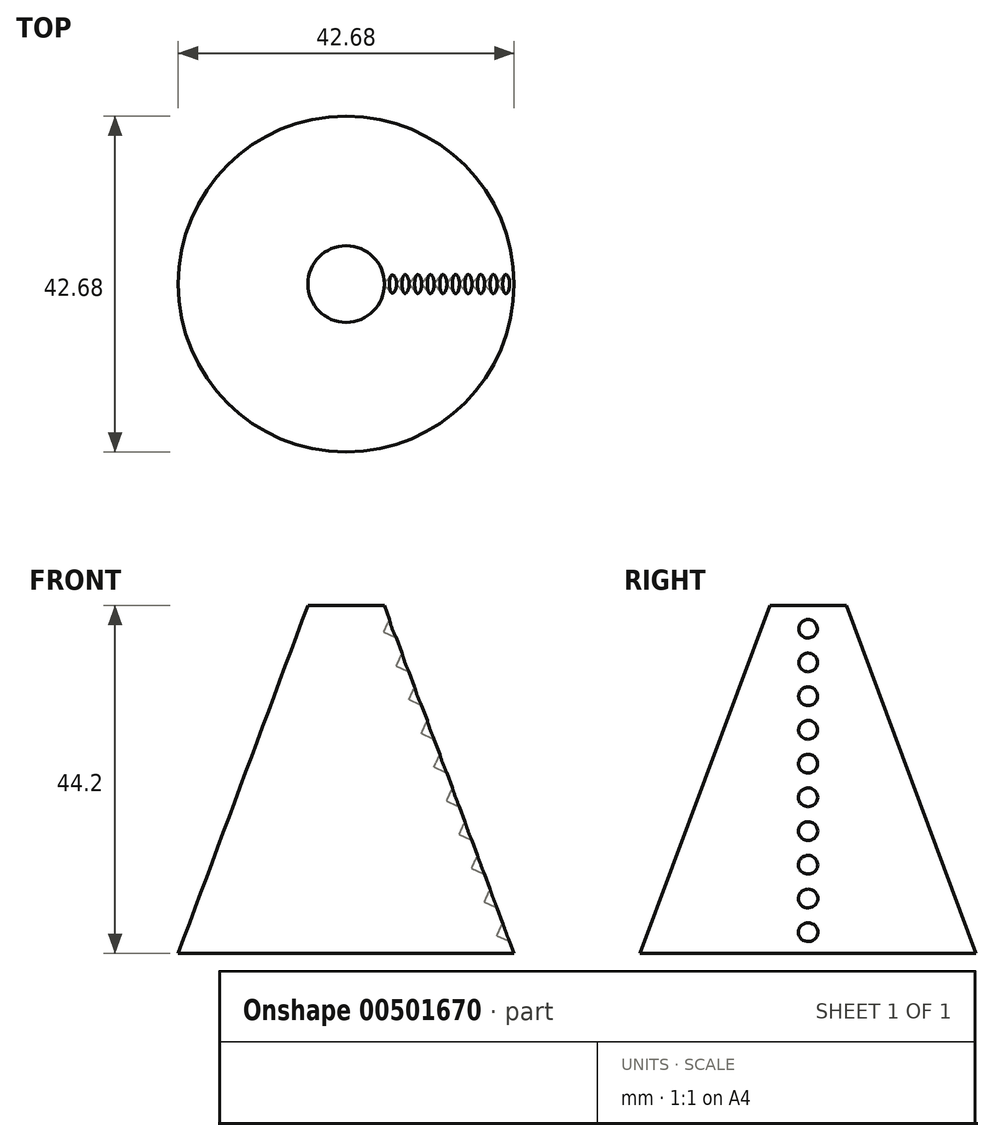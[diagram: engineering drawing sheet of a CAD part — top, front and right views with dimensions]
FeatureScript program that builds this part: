
annotation { "Feature Type Name" : "Feature", "Feature Type Description" : "" }
export const myFeature = defineFeature(function(context is Context, id is Id, definition is map)
    precondition{}
    {
        {
            var Q0;
            Q0=qCreatedBy(makeId("Front.planeOp"),FACE);
            var sketch = newSketch(context, id + "F0", { "sketchPlane" : qUnion([Q0])});
            skLineSegment(sketch, "E0", {"start": v(0, 0) * mm, "end": v(0, 44.2) * mm});
            skLineSegment(sketch, "E1", {"start": v(0, 44.2) * mm, "end": v(4.86, 44.2) * mm});
            skLineSegment(sketch, "E2", {"start": v(4.86, 44.2) * mm, "end": v(21.34, 0) * mm});
            skLineSegment(sketch, "E3", {"start": v(21.34, 0) * mm, "end": v(0, 0) * mm});
            skSolve(sketch);
        }
        {
            var Q0;
            Q0=makeQuery(id+"F0.imprint","IMPRINT",FACE,{"disambiguationData":[TD([[makeQuery(id+"F0.imprint","IMPRINT",EDGE,{"derivedFrom":sQuery(id+"F0.wireOp",EDGE,"E0")}),-1.0]])]});
            var Q1;
            Q1=sQuery(id+"F0.wireOp",EDGE,"E0");
            revolve(context, id + "F1", {"surfaceOperationType" : NewSurfaceOperationType.NEW, "entities" : qUnion([Q0]), "axis" : qUnion([Q1]), "revolveType" : RevolveType.FULL});
        }
        {
            var Q0;
            Q0=sQuery(id+"F0.wireOp",EDGE,"E2");
            cPlane(context, id + "F2", {"entities" : qUnion([Q0]), "cplaneType" : CPlaneType.LINE_ANGLE, "offset" : 25.4 * mm, "angle" : 0 * degree, "width" : 152.4 * mm, "height" : 152.4 * mm});
        }
        {
            var Q0;
            Q0=qCreatedBy(id+"F2.planeOp",FACE);
            var sketch = newSketch(context, id + "F3", { "sketchPlane" : qUnion([Q0])});
            skCircle(sketch, "E4", {"center": v(0, 36.58) * mm, "radius": 1.27 * mm});
            skCircle(sketch, "E5", {"center": v(0, 32) * mm, "radius": 1.27 * mm});
            skCircle(sketch, "E6", {"center": v(0, 27.43) * mm, "radius": 1.27 * mm});
            skCircle(sketch, "E7", {"center": v(0, 22.86) * mm, "radius": 1.27 * mm});
            skCircle(sketch, "E8", {"center": v(0, 18.29) * mm, "radius": 1.27 * mm});
            skCircle(sketch, "E9", {"center": v(0, 13.72) * mm, "radius": 1.27 * mm});
            skCircle(sketch, "E10", {"center": v(0, 9.14) * mm, "radius": 1.27 * mm});
            skCircle(sketch, "E11", {"center": v(0, 0) * mm, "radius": 1.27 * mm});
            skCircle(sketch, "E12", {"center": v(0, 4.57) * mm, "radius": 1.27 * mm});
            skCircle(sketch, "E13", {"center": v(0, -4.57) * mm, "radius": 1.27 * mm});
            skSolve(sketch);
        }
        {
            var Q0;
            Q0=makeQuery(id+"F3.imprint","IMPRINT",FACE,{"disambiguationData":[TD([[makeQuery(id+"F3.imprint","IMPRINT",EDGE,{"derivedFrom":sQuery(id+"F3.wireOp",EDGE,"E4")}),1.0]])]});
            var Q1;
            Q1=makeQuery(id+"F3.imprint","IMPRINT",FACE,{"disambiguationData":[TD([[makeQuery(id+"F3.imprint","IMPRINT",EDGE,{"derivedFrom":sQuery(id+"F3.wireOp",EDGE,"E5")}),1.0]])]});
            var Q2;
            Q2=makeQuery(id+"F3.imprint","IMPRINT",FACE,{"disambiguationData":[TD([[makeQuery(id+"F3.imprint","IMPRINT",EDGE,{"derivedFrom":sQuery(id+"F3.wireOp",EDGE,"E6")}),1.0]])]});
            var Q3;
            Q3=makeQuery(id+"F3.imprint","IMPRINT",FACE,{"disambiguationData":[TD([[makeQuery(id+"F3.imprint","IMPRINT",EDGE,{"derivedFrom":sQuery(id+"F3.wireOp",EDGE,"E7")}),1.0]])]});
            var Q4;
            Q4=makeQuery(id+"F3.imprint","IMPRINT",FACE,{"disambiguationData":[TD([[makeQuery(id+"F3.imprint","IMPRINT",EDGE,{"derivedFrom":sQuery(id+"F3.wireOp",EDGE,"E8")}),1.0]])]});
            var Q5;
            Q5=makeQuery(id+"F3.imprint","IMPRINT",FACE,{"disambiguationData":[TD([[makeQuery(id+"F3.imprint","IMPRINT",EDGE,{"derivedFrom":sQuery(id+"F3.wireOp",EDGE,"E9")}),1.0]])]});
            var Q6;
            Q6=makeQuery(id+"F3.imprint","IMPRINT",FACE,{"disambiguationData":[TD([[makeQuery(id+"F3.imprint","IMPRINT",EDGE,{"derivedFrom":sQuery(id+"F3.wireOp",EDGE,"E10")}),1.0]])]});
            var Q7;
            Q7=makeQuery(id+"F3.imprint","IMPRINT",FACE,{"disambiguationData":[TD([[makeQuery(id+"F3.imprint","IMPRINT",EDGE,{"derivedFrom":sQuery(id+"F3.wireOp",EDGE,"E12")}),1.0]])]});
            var Q8;
            Q8=makeQuery(id+"F3.imprint","IMPRINT",FACE,{"disambiguationData":[TD([[makeQuery(id+"F3.imprint","IMPRINT",EDGE,{"derivedFrom":sQuery(id+"F3.wireOp",EDGE,"E11")}),1.0]])]});
            var Q9;
            Q9=makeQuery(id+"F3.imprint","IMPRINT",FACE,{"disambiguationData":[TD([[makeQuery(id+"F3.imprint","IMPRINT",EDGE,{"derivedFrom":sQuery(id+"F3.wireOp",EDGE,"E13")}),1.0]])]});
            extrude(context, id + "F4", {"entities" : qUnion([Q0, Q1, Q2, Q3, Q4, Q5, Q6, Q7, Q8, Q9]), "operationType" : NewBodyOperationType.REMOVE, "depth" : 2.54 * mm, "offsetDistance" : 25.4 * mm, "hasDraft" : true, "draftAngle" : 45 * degree, "draftPullDirection" : true, "hasSecondDirection" : true, "secondDirectionOppositeDirection" : true, "secondDirectionDepth" : 2.54 * mm, "hasSecondDirectionDraft" : true, "secondDirectionDraftAngle" : 45 * degree});
        }
    });
